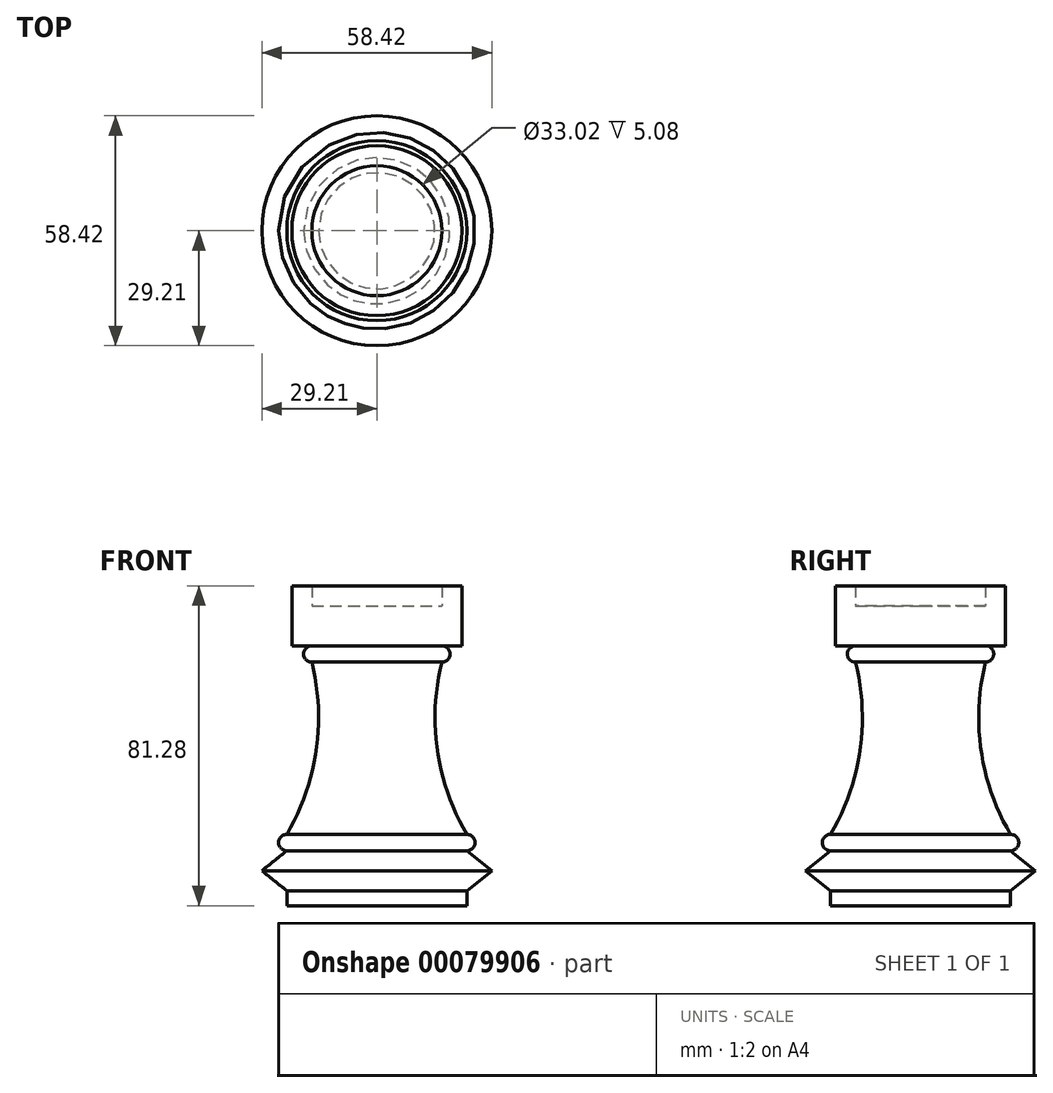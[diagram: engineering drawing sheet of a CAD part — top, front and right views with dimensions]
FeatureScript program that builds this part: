
annotation { "Feature Type Name" : "Feature", "Feature Type Description" : "" }
export const myFeature = defineFeature(function(context is Context, id is Id, definition is map)
    precondition{}
    {
        {
            var Q0;
            Q0=qCreatedBy(makeId("Front.planeOp"),FACE);
            var sketch = newSketch(context, id + "F0", { "sketchPlane" : qUnion([Q0])});
            skLineSegment(sketch, "E0", {"start": v(0, 76.2) * mm, "end": v(0, 0) * mm});
            skLineSegment(sketch, "E1", {"start": v(0, 0) * mm, "end": v(0, 76.2) * mm});
            skLineSegment(sketch, "E2", {"start": v(0, 76.2) * mm, "end": v(16.51, 76.2) * mm});
            skLineSegment(sketch, "E3", {"start": v(16.51, 76.2) * mm, "end": v(16.51, 81.28) * mm});
            skLineSegment(sketch, "E4", {"start": v(16.51, 81.28) * mm, "end": v(21.59, 81.28) * mm});
            skLineSegment(sketch, "E5", {"start": v(21.59, 81.28) * mm, "end": v(21.59, 66.04) * mm});
            skLineSegment(sketch, "E6", {"start": v(21.59, 66.04) * mm, "end": v(16.51, 66.04) * mm});
            skArc(sketch, "E7", {"start": v(16.51, 61.87) * mm, "mid": v(18.6, 63.96) * mm, "end": v(16.51, 66.04) * mm});
            skArc(sketch, "E8", {"start": v(16.51, 61.87) * mm, "mid": v(15.39, 39.38) * mm, "end": v(22.86, 18.14) * mm});
            skArc(sketch, "E9", {"start": v(22.86, 13.97) * mm, "mid": v(24.94, 16.05) * mm, "end": v(22.86, 18.14) * mm});
            skLineSegment(sketch, "E10", {"start": v(22.86, 13.97) * mm, "end": v(29.21, 8.9) * mm});
            skLineSegment(sketch, "E11", {"start": v(29.21, 8.89) * mm, "end": v(22.86, 3.8) * mm});
            skLineSegment(sketch, "E12", {"start": v(22.86, 3.81) * mm, "end": v(22.86, 0) * mm});
            skLineSegment(sketch, "E13", {"start": v(22.86, 0) * mm, "end": v(0, 0) * mm});
            skSolve(sketch);
        }
        {
            var Q0;
            Q0 = qSketchRegion(id + "F0", true);
            var Q1;
            Q1=sQuery(id+"F0.wireOp",EDGE,"E1");
            revolve(context, id + "F1", {"entities" : qUnion([Q0]), "axis" : qUnion([Q1]), "revolveType" : RevolveType.FULL});
        }
    });
